# Revit family: Faucet-Bradley_Corp-Deck_Mounted-Verge_Linea-S53-3500
name_source: partatom
category: Plumbing Fixtures
revit_build: Autodesk Revit 2018 (Build: 20170223_1515(x64)
units: mm (PartAtom-declared; Revit-internal decimal feet)

## family parameters
Cut with Voids When Loaded = No
Host = Face
Part Type = Normal
Room Calculation Point = No
Round Connector Dimension = Use Diameter
Shared = No

## types (1)
- Verge Linea Series S53-3500
    ADA Compliant = Yes
    Default Elevation = 36"
    Description = Touchless Deck Mounted Verge Linea Series S53-3500 Faucet, Paired with Linea Series 6-3500 Soap Dispenser
    Installation Type = Deck Mounted
    Manufacturer = Bradley Corporation
    Manufacturer Installation URL - English = https://www.bradleycorp.com
    Model = Verge Linea Series S53-3500
    Product Page URL = https://www.bradleycorp.com
    Product Tech Data URL - English = https://www.bradleycorp.com
    Specifications URL = https://www.bradleycorp.com
    Type Comments = Touchless Deck Mounted Verge Linea Series S53-3500 Faucet, Paired with Linea Series 6-3500 Soap Dispenser

## geometry (parser evidence)
native form markers: Sweep x1
no freeform markers — native parametric forms only
